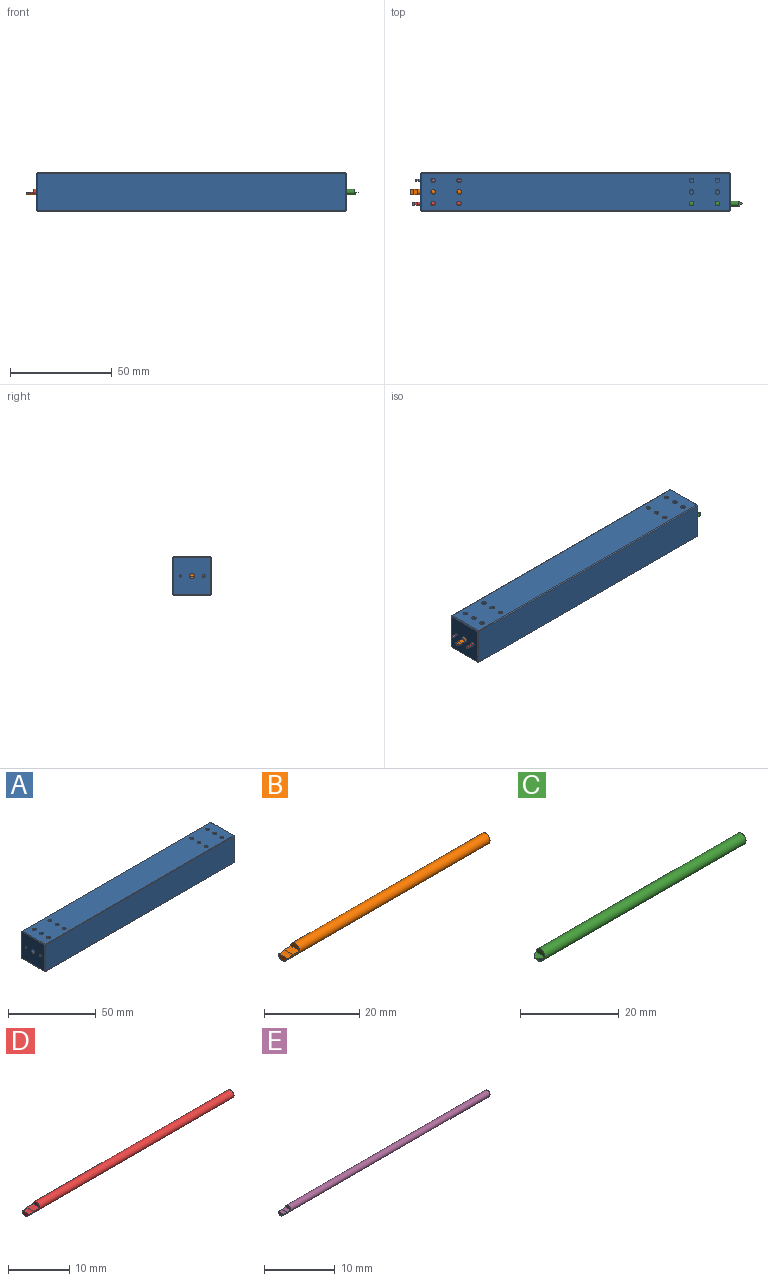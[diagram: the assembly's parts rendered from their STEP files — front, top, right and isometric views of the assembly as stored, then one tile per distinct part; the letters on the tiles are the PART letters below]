
ASSEMBLY  parts=5 mates=4
PART A: 58 faces, bbox 152.4x19.1x19.1 mm
  f0: cylinder r=0.51mm len=41.28mm, axis (-1,0,0), area 127.4mm2, adj f7,f12,f32,f33,f35,f36
  f1: cylinder r=0.76mm len=44.45mm, axis (-1,0,0), area 205.9mm2, adj f7,f13,f26,f27,f28,f29,f30,f31
  f2: cylinder r=1.27mm len=57.15mm, axis (-1,0,0), area 446.8mm2, adj f7,f14,f24,f25
  f3: cylinder r=1.27mm len=57.15mm, axis (1,0,0), area 446.8mm2, adj f9,f15,f22,f23
  f4: cylinder r=1.59mm len=63.5mm, axis (1,0,0), area 624.7mm2, adj f9,f16,f20,f21
  f5: cylinder r=2.65mm len=88.9mm, axis (1,0,0), area 1474.4mm2, adj f9,f17,f18,f19
  f6: plane 151.64x18.29mm, normal (0,1,0), area 2773.2mm2, adj f41,f42,f51,f52
  f7: plane 18.29x18.29mm, normal (-1,0,0), area 326.7mm2, adj f0,f1,f2,f38,f41,f45,f46
  f8: plane 151.64x18.29mm, normal (0,-1,0), area 2773.2mm2, adj f44,f45,f53,f54
  f9: plane 18.29x18.29mm, normal (1,0,0), area 299.3mm2, adj f3,f4,f5,f43,f52,f53,f57
  f10: plane 151.64x18.29mm, normal (0,0,-1), area 2773.2mm2, adj f38,f42,f43,f44
  f11: plane 151.64x18.29mm, normal (0,0,1), area 2725mm2, adj f18,f19,f20,f21,f22,f23,f24,f25
  f12: plane 1.02x1.02mm, normal (-1,0,0), area 0.8mm2, adj f0
  f13: plane 1.52x1.52mm, normal (-1,0,0), area 1.8mm2, adj f1
  f14: plane 2.54x2.54mm, normal (-1,0,0), area 5.1mm2, adj f2
  f15: plane 2.54x2.54mm, normal (1,0,0), area 5.1mm2, adj f3
  f16: plane 3.18x3.18mm, normal (1,0,0), area 7.9mm2, adj f4
  f17: plane 5.31x5.31mm, normal (1,0,0), area 22.1mm2, adj f5
  f18: cylinder r=1.13mm len=7.13mm, axis (0,0,1), area 49.7mm2, adj f5,f11
  f19: cylinder r=1.13mm len=7.13mm, axis (0,0,1), area 49.7mm2, adj f5,f11
  f20: cylinder r=1.13mm len=8.41mm, axis (0,0,1), area 58mm2, adj f4,f11
  f21: cylinder r=1.13mm len=8.41mm, axis (0,0,1), area 58mm2, adj f4,f11
  f22: cylinder r=1.13mm len=8.95mm, axis (0,0,1), area 60.8mm2, adj f3,f11
  f23: cylinder r=1.13mm len=8.95mm, axis (0,0,1), area 60.8mm2, adj f3,f11
  f24: cylinder r=1.13mm len=8.96mm, axis (0,0,1), area 60.8mm2, adj f2,f11
  f25: cylinder r=1.13mm len=8.96mm, axis (0,0,1), area 60.8mm2, adj f2,f11
  f26: cone r=0mm half-angle=59deg, axis (0,0,1), area 0.7mm2, adj f1,f28
  f27: cone r=0mm half-angle=59deg, axis (0,0,1), area 0.7mm2, adj f1,f28
  f28: cylinder r=1.13mm len=9.02mm, axis (0,0,1), area 63.7mm2, adj f1,f11,f26,f27
  f29: cone r=0mm half-angle=59deg, axis (0,0,1), area 0.7mm2, adj f1,f31
  f30: cone r=0mm half-angle=59deg, axis (0,0,1), area 0.7mm2, adj f1,f31
  f31: cylinder r=1.13mm len=9.02mm, axis (0,0,1), area 63.7mm2, adj f1,f11,f29,f30
  f32: cone r=0mm half-angle=59deg, axis (0,0,1), area 1.3mm2, adj f0,f34
  f33: cone r=0mm half-angle=59deg, axis (0,0,1), area 1.3mm2, adj f0,f34
  f34: cylinder r=1.13mm len=9.02mm, axis (0,0,1), area 64mm2, adj f11,f32,f33
  f35: cone r=0mm half-angle=59deg, axis (0,0,1), area 1.3mm2, adj f0,f37
  f36: cone r=0mm half-angle=59deg, axis (0,0,1), area 1.3mm2, adj f0,f37
  f37: cylinder r=1.13mm len=9.02mm, axis (0,0,1), area 64mm2, adj f11,f35,f36
  f38: plane 18.29x0.38mm, normal (-0.71,0,-0.71), area 9.9mm2, adj f7,f10,f39,f40
  f39: plane 0.38x0.38mm, normal (-0.58,0.58,-0.58), area 0.1mm2, adj f38,f41,f42
  f40: plane 0.38x0.38mm, normal (-0.58,-0.58,-0.58), area 0.1mm2, adj f38,f44,f45
  f41: plane 18.29x0.38mm, normal (-0.71,0.71,0), area 9.9mm2, adj f6,f7,f39,f47
  f42: plane 151.64x0.38mm, normal (0,0.71,-0.71), area 81.7mm2, adj f6,f10,f39,f48
  f43: plane 18.29x0.38mm, normal (0.71,0,-0.71), area 9.9mm2, adj f9,f10,f48,f49
  f44: plane 151.64x0.38mm, normal (0,-0.71,-0.71), area 81.7mm2, adj f8,f10,f40,f49
  f45: plane 18.29x0.38mm, normal (-0.71,-0.71,0), area 9.9mm2, adj f7,f8,f40,f50
  f46: plane 18.29x0.38mm, normal (-0.71,0,0.71), area 9.9mm2, adj f7,f11,f47,f50
  f47: plane 0.38x0.38mm, normal (-0.58,0.58,0.58), area 0.1mm2, adj f41,f46,f51
  f48: plane 0.38x0.38mm, normal (0.58,0.58,-0.58), area 0.1mm2, adj f42,f43,f52
  f49: plane 0.38x0.38mm, normal (0.58,-0.58,-0.58), area 0.1mm2, adj f43,f44,f53
  f50: plane 0.38x0.38mm, normal (-0.58,-0.58,0.58), area 0.1mm2, adj f45,f46,f54
  f51: plane 151.64x0.38mm, normal (0,0.71,0.71), area 81.7mm2, adj f6,f11,f47,f55
  f52: plane 18.29x0.38mm, normal (0.71,0.71,0), area 9.9mm2, adj f6,f9,f48,f55
  f53: plane 18.29x0.38mm, normal (0.71,-0.71,0), area 9.9mm2, adj f8,f9,f49,f56
  f54: plane 151.64x0.38mm, normal (0,-0.71,0.71), area 81.7mm2, adj f8,f11,f50,f56
  f55: plane 0.38x0.38mm, normal (0.58,0.58,0.58), area 0.1mm2, adj f51,f52,f57
  f56: plane 0.38x0.38mm, normal (0.58,-0.58,0.58), area 0.1mm2, adj f53,f54,f57
  f57: plane 18.29x0.38mm, normal (0.71,0,0.71), area 9.9mm2, adj f9,f11,f55,f56
PART B: 6 faces, bbox 60.3x2.5x2.5 mm
  f0: cylinder r=1.27mm len=60.33mm, axis (-1,0,0), area 465.3mm2, adj f1,f2,f3,f4,f5
  f1: plane 2.54x1.91mm, normal (0,0,1), area 4.8mm2, adj f0,f4,f5
  f2: plane 2.54x2.54mm, normal (1,0,0), area 5.1mm2, adj f0
  f3: plane 2.54x1.27mm, normal (-1,0,0), area 2.5mm2, adj f0,f5
  f4: plane 2.54x1.27mm, normal (-1,0,0), area 2.5mm2, adj f0,f1
  f5: cylinder r=1.59mm len=2.54mm, axis (0,1,0), area 5.1mm2, adj f0,f1,f3
PART C: 5 faces, bbox 59.4x2.5x2.5 mm
  f0: cylinder r=1.27mm len=58.13mm, axis (-1,0,0), area 461.3mm2, adj f1,f2,f3,f4
  f1: cone r=1.27mm half-angle=45deg, axis (1,0,0), area 3.6mm2, adj f0,f4
  f2: plane 2.54x2.54mm, normal (1,0,0), area 5.1mm2, adj f0
  f3: plane 2.54x1.27mm, normal (-1,0,0), area 2.5mm2, adj f0,f4
  f4: plane 2.54x1.91mm, normal (0,0,1), area 3.2mm2, adj f0,f1,f3
PART D: 6 faces, bbox 47.6x1.5x1.5 mm
  f0: cylinder r=0.76mm len=47.63mm, axis (-1,0,0), area 221.6mm2, adj f1,f2,f3,f4,f5
  f1: plane 1.52x1.4mm, normal (0,0,1), area 2.1mm2, adj f0,f4,f5
  f2: plane 1.52x1.52mm, normal (1,0,0), area 1.8mm2, adj f0
  f3: plane 1.52x0.76mm, normal (-1,0,0), area 0.9mm2, adj f0,f5
  f4: plane 1.52x0.76mm, normal (-1,0,0), area 0.9mm2, adj f0,f1
  f5: cylinder r=0.95mm len=1.52mm, axis (0,1,0), area 1.8mm2, adj f0,f1,f3
PART E: 6 faces, bbox 41.3x1x1 mm
  f0: plane 1.02x0.51mm, normal (-1,0,0), area 0.4mm2, adj f1,f5
  f1: cylinder r=0.51mm len=41.28mm, axis (-1,0,0), area 129.2mm2, adj f0,f2,f3,f4,f5
  f2: plane 1.02x1.02mm, normal (1,0,0), area 0.8mm2, adj f1
  f3: plane 1.02x0.76mm, normal (0,0,1), area 0.8mm2, adj f1,f4,f5
  f4: plane 1.02x0.51mm, normal (-1,0,0), area 0.4mm2, adj f1,f3
  f5: cylinder r=0.64mm len=1.02mm, axis (0,-1,0), area 0.8mm2, adj f0,f1,f3
PLACE A t=(34.29,-1.52,37.43)mm
PLACE B t=(-46.99,2.29,27.91)mm
PLACE C rot(axis=(0,0,1),180deg) t=(114.93,-15.96,27.91)mm
PLACE D t=(-45.72,-7.24,27.91)mm
PLACE E t=(-44.45,0.38,27.91)mm
MATE fastened C.f0 <-> A.f1  axis (-1,0,0) through (115.57,-7.24,27.91)mm
MATE fastened B.f0 <-> A.f2  axis (-1,0,0) through (-46.99,-1.52,27.91)mm
MATE fastened D.f0 <-> A.f1  axis (-1,0,0) through (-45.72,-7.24,27.91)mm
MATE fastened E.f1 <-> A.f0  axis (-1,0,0) through (-44.45,4.19,27.91)mm
